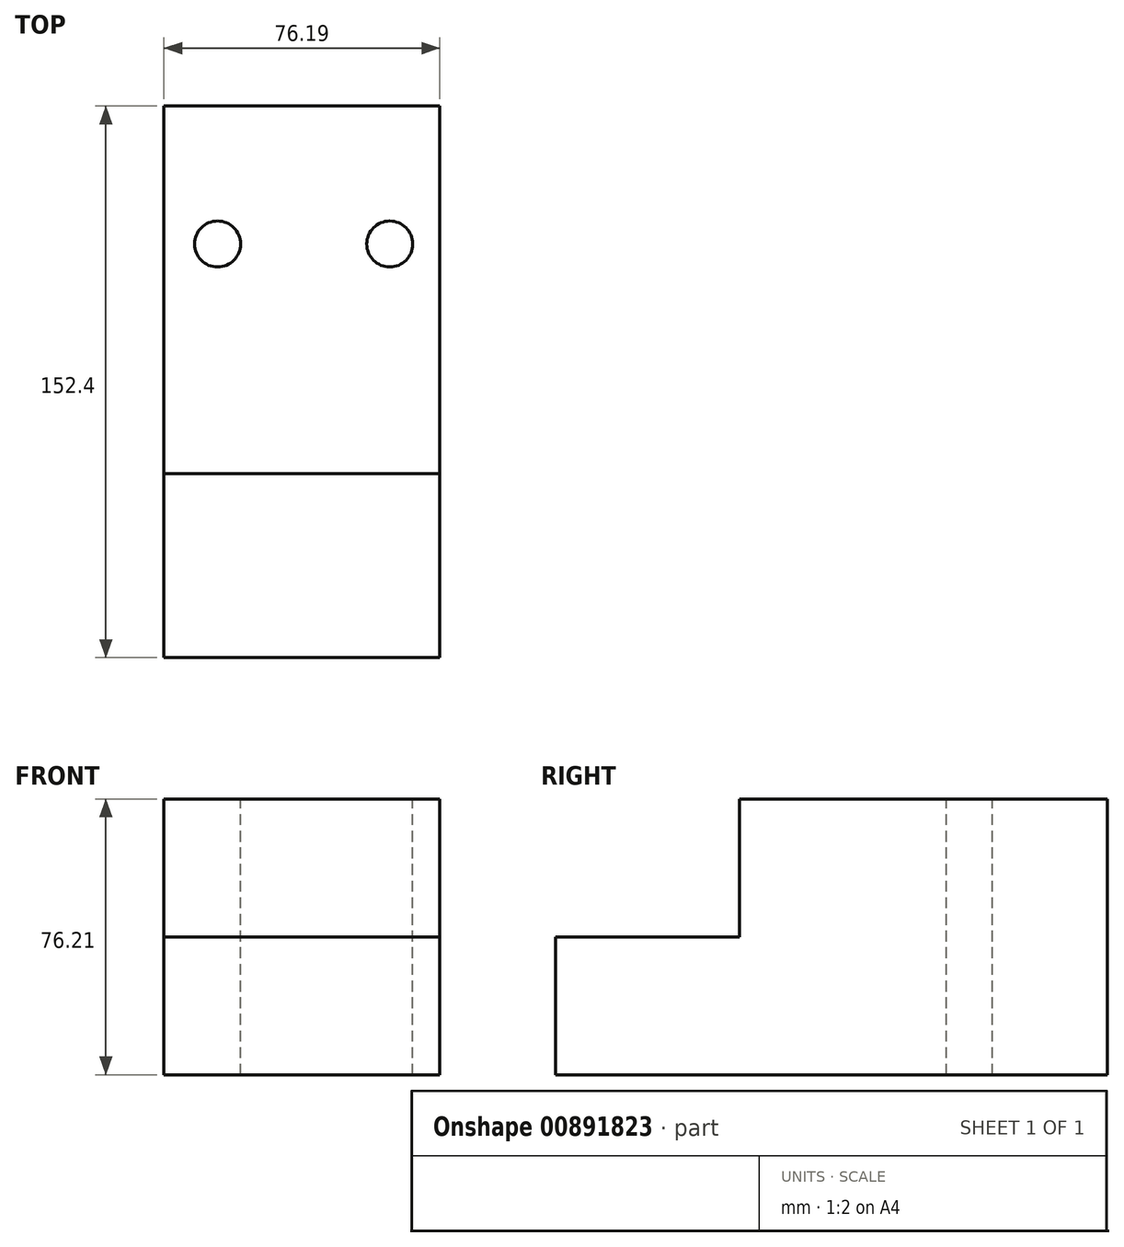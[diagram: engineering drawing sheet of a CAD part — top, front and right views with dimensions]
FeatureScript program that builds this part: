
annotation { "Feature Type Name" : "Feature", "Feature Type Description" : "" }
export const myFeature = defineFeature(function(context is Context, id is Id, definition is map)
    precondition{}
    {
        {
            var Q0;
            Q0=qCreatedBy(makeId("Front.planeOp"),FACE);
            var sketch = newSketch(context, id + "F0", { "sketchPlane" : qUnion([Q0])});
            skLineSegment(sketch, "E0", {"start": v(-45.25, 39.67) * mm, "end": v(30.94, 39.67) * mm});
            skLineSegment(sketch, "E1", {"start": v(30.94, 39.67) * mm, "end": v(30.94, -36.54) * mm});
            skLineSegment(sketch, "E2", {"start": v(-45.25, -36.54) * mm, "end": v(30.94, -36.54) * mm});
            skLineSegment(sketch, "E3", {"start": v(-45.25, -36.54) * mm, "end": v(-45.25, 39.67) * mm});
            skSolve(sketch);
        }
        {
            var Q0;
            Q0=qSketchRegion(id+"F0",true);
            extrude(context, id + "F1", {"entities" : qUnion([Q0]), "depth" : 152.4 * mm, "offsetDistance" : 25.4 * mm});
        }
        {
            var Q0;
            Q0=makeQuery(id+"F1.opExtrude","SWEPT_FACE",FACE,{"disambiguationData":[OSD([sQuery(id+"F0.wireOp",EDGE,"E1")])]});
            var sketch = newSketch(context, id + "F2", { "sketchPlane" : qUnion([Q0])});
            skLineSegment(sketch, "E4", {"start": v(-152.4, 39.67) * mm, "end": v(-152.4, 1.57) * mm});
            skLineSegment(sketch, "E5", {"start": v(-152.4, 1.57) * mm, "end": v(-101.59, 1.57) * mm});
            skLineSegment(sketch, "E6", {"start": v(-101.59, 1.57) * mm, "end": v(-101.59, 39.67) * mm});
            skLineSegment(sketch, "E7", {"start": v(-101.59, 39.67) * mm, "end": v(-152.4, 39.67) * mm});
            skSolve(sketch);
        }
        {
            var Q0;
            Q0=qSketchRegion(id+"F2",true);
            extrude(context, id + "F3", {"entities" : qUnion([Q0]), "operationType" : NewBodyOperationType.REMOVE, "oppositeDirection" : true, "depth" : 76.2 * mm, "offsetDistance" : 25.4 * mm});
        }
        {
            var Q0;
            Q0=makeQuery(id+"F1.opExtrude","SWEPT_FACE",FACE,{"disambiguationData":[OSD([sQuery(id+"F0.wireOp",EDGE,"E0")])]});
            var sketch = newSketch(context, id + "F4", { "sketchPlane" : qUnion([Q0])});
            skCircle(sketch, "E8", {"center": v(-30.43, -38.1) * mm, "radius": 6.35 * mm});
            skCircle(sketch, "E9", {"center": v(17.12, -38.1) * mm, "radius": 6.35 * mm});
            skSolve(sketch);
        }
        {
            var Q0;
            Q0=qSketchRegion(id+"F4",true);
            extrude(context, id + "F5", {"entities" : qUnion([Q0]), "operationType" : NewBodyOperationType.REMOVE, "oppositeDirection" : true, "depth" : 101.6 * mm, "offsetDistance" : 25.4 * mm});
        }
    });
